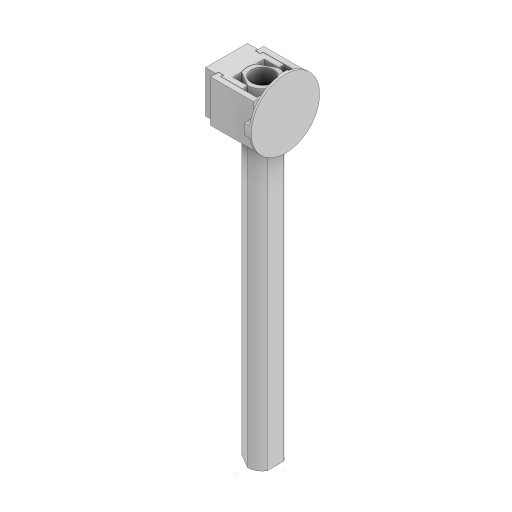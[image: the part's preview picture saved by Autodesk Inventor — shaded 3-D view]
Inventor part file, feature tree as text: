
AUTODESK INVENTOR PART (.ipt)
format: ipt  version: 2024 (Build 280153000, 153)  size: 452,608 bytes
history: native  units: in
note: dims shown in document units (in); Inventor stores cm internally (conversion verified against a paired STEP export)
features: sketch x15, extrude x13, projected_geometry x2
ambient origin geometry x8: Origin, YZ Plane, XZ Plane, XY Plane, X Axis, Y Axis, Z Axis, Center Point
bodies: Solid1 (feature_tree), Solid2 (feature_tree), Solid3 (feature_tree), Solid4 (feature_tree)
feature tree (30):
  extrude  "Extrusion1"  Depth=0.315in
  extrude  "Extrusion2"  Depth=1.1811in TaperAngle=360.0deg
  extrude  "Extrusion3"  Depth=12.4016in
  extrude  "Extrusion4"  Depth=1.378in
  extrude  "Extrusion5"  Depth=1.5748in TaperAngle=0.0deg
  extrude  "Extrusion6"  Depth=0.0098in
  sketch  "Sketch7"  dims[d25=90.0deg d26=90.0deg]
  extrude  "Extrusion7"  TaperAngle=90.0deg  [1 undecoded]
  extrude  "Extrusion8"  Depth=0.2067in
  extrude  "Extrusion9"  Depth=1.5748in TaperAngle=0.0deg
  sketch  "Sketch11"  dims[d34=0.1373in d35=0.0in d36=0.0098in]
  extrude  "Extrusion10"  Depth=0.2165in
  extrude  "Extrusion11"  Depth=0.0098in
  extrude  "Extrusion12"  Depth=2.5591in
  extrude  "Extrusion13"  Depth=0.0787in TaperAngle=0.0deg
  sketch  "Sketch1"  dims[d6=0.315in d7=0.315in]
  sketch  "Sketch2"  dims[d8=0.8476in d9=1.1811in d11=360.0deg]
  sketch  "Sketch3"  dims[d13=12.4016in d14=0.0in d15=0.0079in]
  sketch  "Sketch4"  dims[d18=0.1969in d19=1.378in]
  sketch  "Sketch5"  dims[d20=0.1969in d21=1.5748in d22=0.0in]
  sketch  "Sketch6"  dims[d23=0.0098in d24=0.0098in]
  projected_geometry  "Projected Loop1"
  sketch  "Sketch8"  dims[d27=0.0984in d28=0.2067in]
  sketch  "Sketch9"  dims[d29=0.0787in d30=1.5748in d31=0.0in]
  sketch  "Sketch10"  dims[d32=0.2165in d33=0.2165in]
  projected_geometry  "Projected Loop2"
  sketch  "Sketch12"  dims[d37=0.2362in d38=0.0in d39=2.5591in]
  sketch  "Sketch13"  dims[d40=0.0787in d41=0.0in d42=0.0925in d43=0.0in]
  sketch  "Sketch14"  dims[d44=0.1216in d45=0.0in]
  sketch  "Sketch15"  dims[d46=0.1772in d47=0.1772in d48=0.2466in d49=0.0in d50=0.2795in d52=0.1969in d53=0.1969in d54=0.0in d56=0.1969in d57=0.1969in d58=0.1969in d59=0.0in d60=0.002in d61=0.002in d62=0.1969in d63=0.0in d64=0.1575in d65=0.0in]
note: 1 required parameter value undecoded (feature->parameter linkage not recoverable at this tier; creation-order binding heuristic only, values carry confidence <= 0.55)
